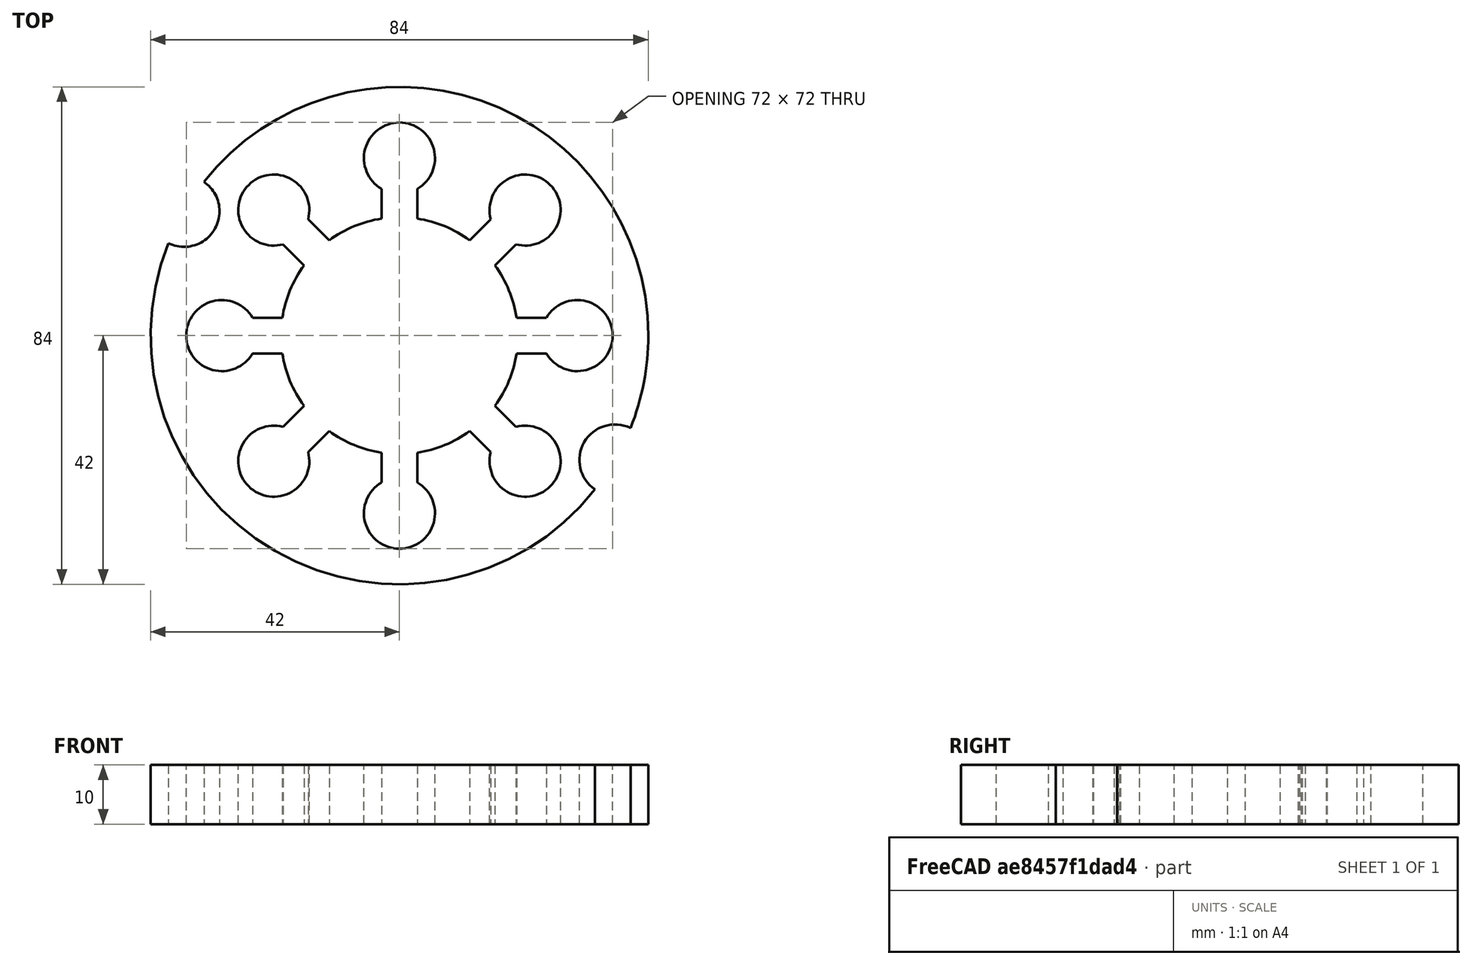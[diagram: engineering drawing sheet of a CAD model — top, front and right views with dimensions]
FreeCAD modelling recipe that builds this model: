
FCSTD DOCUMENT  (FreeCAD 0.18R4 (GitTag))
Label: Assignment 3 Templates 2
License: All rights reserved
LicenseURL: http://en.wikipedia.org/wiki/All_rights_reserved
objects: TechDraw::DrawViewDimension×8, TechDraw::DrawViewAnnotation×4, Sketcher::SketchObject×3, TechDraw::DrawViewPart×3, PartDesign::Pocket×2, PartDesign::Pad×1, PartDesign::PolarPattern×1, PartDesign::Body×1, TechDraw::DrawSVGTemplate×1, TechDraw::DrawPage×1
note: 11 computed .brp shape members not serialized (recipe doc carries the construction recipe); baked Part::Feature solids carry a one-line shape summary decoded from their .brp

FEATURE [Sketcher::SketchObject] Sketch
  MapMode = 5
  Support = -> [XY_Plane]
  sketch-geometry (2):
    g0: Circle CenterX=0 CenterY=0 CenterZ=0 NormalX=0 NormalY=0 NormalZ=1 AngleXU=0 Radius=42
    g1: Circle CenterX=0 CenterY=0 CenterZ=0 NormalX=0 NormalY=0 NormalZ=1 AngleXU=0 Radius=20
  constraints (4):
    c: Coincident(g0,g1)
    c: Coincident(g0,g-1)
    c: Radius(g0) = 42
    c: Radius(g1) = 20
FEATURE [PartDesign::Pad] Pad
  Length = 10
  Length2 = 100
  Profile = -> Sketch
  Type = 0
FEATURE [Sketcher::SketchObject] Sketch001
  MapMode = 5
  Placement = pos=(0,0,10) rot=(0,0,1;0rad)
  Support = -> [Pad]
  sketch-geometry (2):
    g0: Circle CenterX=-36.37 CenterY=21 CenterZ=0 NormalX=0 NormalY=0 NormalZ=1 AngleXU=0 Radius=6
    g1: Circle CenterX=36.37 CenterY=-21 CenterZ=0 NormalX=0 NormalY=0 NormalZ=1 AngleXU=0 Radius=6
  constraints (5):
    c: Symmetric(g1,g0,g-1)
    c: Radius(g1) = 6
    c: Radius(g0) = 6
    c: DistanceY(g-1,g0) = 21
    c: DistanceX(g-1,g1) = 36.37
FEATURE [PartDesign::Pocket] Pocket
  BaseFeature = -> Pad
  Length = 5
  Length2 = 100
  Profile = -> Sketch001
  Type = 1
FEATURE [Sketcher::SketchObject] Sketch002
  MapMode = 5
  Placement = pos=(0,0,10) rot=(0,0,1;0rad)
  Support = -> [Pocket]
  sketch-geometry (4):
    g0: ArcOfCircle CenterX=0 CenterY=30 CenterZ=0 NormalX=0 NormalY=0 NormalZ=1 AngleXU=0 Radius=6 StartAngle=5.23599 EndAngle=10.472
    g1: LineSegment StartX=-3 StartY=24.8038 StartZ=0 EndX=-3 EndY=19.7737 EndZ=0
    g2: LineSegment StartX=3 StartY=24.8038 StartZ=0 EndX=3 EndY=19.7737 EndZ=0
    g3: ArcOfCircle CenterX=0 CenterY=0 CenterZ=0 NormalX=0 NormalY=0 NormalZ=1 AngleXU=0 Radius=20 StartAngle=1.42023 EndAngle=1.72136
  constraints (12):
    c: Radius(g0) = 6
    c: DistanceY(g-1,g0) = 30
    c: PointOnObject(g0,g-2)
    c: Radius(g3) = 20
    c: Coincident(g-1,g3)
    c: Vertical(g1)
    c: Vertical(g2)
    c: PointOnObject(g0,g2)
    c: PointOnObject(g0,g1)
    c: Coincident(g3,g2)
    c: Coincident(g3,g1)
    c: DistanceX(g0,g0) = 6
FEATURE [PartDesign::Pocket] Pocket001
  BaseFeature = -> Pocket
  Length = 5
  Length2 = 100
  Profile = -> Sketch002
  Type = 1
FEATURE [PartDesign::PolarPattern] PolarPattern
  Angle = 360
  Axis = -> Sketch002 [N_Axis]
  BaseFeature = -> Pocket001
  Occurrences = 8
  Originals = -> [Pocket001]
FEATURE [PartDesign::Body] Body
  Group = -> [Sketch,Pad,Sketch001,Pocket,Sketch002,Pocket001,PolarPattern]
  Origin = -> Origin
  Tip = -> PolarPattern
FEATURE [TechDraw::DrawSVGTemplate] Template
  EditableTexts = Designed_by_Name=Soumojit Shome; Drawing_number=Drawing number- 03; FC-Date=15/11/2022; FC-SC=1:1; FC-SH=03; FC-Title=Academy of Technology; Subtitle=ECE-3 (X) ROLL - 139; Weight=Weight
  Height = 210
  Orientation = 1
  Width = 297
FEATURE [TechDraw::DrawViewPart] View
  CoarseView = false
  Direction = (0,0,1)
  Focus = 100
  HardHidden = false
  IsoCount = 0
  IsoHidden = false
  IsoVisible = false
  LockPosition = false
  Perspective = false
  Rotation = 0
  ScaleType = 0
  SeamHidden = false
  SeamVisible = false
  SmoothHidden = false
  SmoothVisible = false
  Source = -> [PolarPattern]
  X = 79.1917
  Y = 87.7641
FEATURE [TechDraw::DrawViewPart] View001
  CoarseView = false
  Direction = (0,-1,0)
  Focus = 100
  HardHidden = false
  IsoCount = 0
  IsoHidden = false
  IsoVisible = false
  LockPosition = false
  Perspective = false
  Rotation = 0
  ScaleType = 0
  SeamHidden = false
  SeamVisible = false
  SmoothHidden = false
  SmoothVisible = false
  Source = -> [PolarPattern]
  X = 77.2612
  Y = 182.602
FEATURE [TechDraw::DrawViewAnnotation] Annotation
  Font = osifont
  LineSpace = 80
  LockPosition = false
  MaxWidth = -1
  Rotation = 0
  ScaleType = 0
  Text = Front View
  TextSize = 6
  TextStyle = 0
  X = 78.4686
  Y = 164.472
FEATURE [TechDraw::DrawViewAnnotation] Annotation001
  Font = osifont
  LineSpace = 80
  LockPosition = false
  MaxWidth = -1
  Rotation = 0
  ScaleType = 0
  Text = Top View
  TextSize = 6
  TextStyle = 0
  X = 79.0471
  Y = 28.4477
FEATURE [TechDraw::DrawViewPart] View002
  CoarseView = false
  Direction = (0.577,-0.577,0.577)
  Focus = 100
  HardHidden = false
  IsoCount = 0
  IsoHidden = false
  IsoVisible = false
  LockPosition = false
  Perspective = false
  Rotation = 0
  ScaleType = 0
  SeamHidden = false
  SeamVisible = false
  SmoothHidden = false
  SmoothVisible = false
  Source = -> [PolarPattern]
  X = 217.907
  Y = 138.113
FEATURE [TechDraw::DrawViewAnnotation] Annotation002
  Font = osifont
  LineSpace = 80
  LockPosition = false
  MaxWidth = -1
  Rotation = 0
  ScaleType = 0
  Text = Isometric View
  TextSize = 6
  TextStyle = 0
  X = 220.835
  Y = 91.701
FEATURE [TechDraw::DrawViewDimension] Dimension
  Arbitrary = false
  FormatSpec = %.2f
  LockPosition = false
  MeasureType = 1
  OverTolerance = 0
  References2D = -> [View001]
  Rotation = 0
  ScaleType = 0
  Type = 2
  UnderTolerance = 0
  X = 59.4308
  Y = -17.4308
FEATURE [TechDraw::DrawViewDimension] Dimension001
  Arbitrary = false
  FormatSpec = R%.2f
  LockPosition = false
  MeasureType = 1
  OverTolerance = 0
  References2D = -> [View]
  Rotation = 0
  ScaleType = 0
  Type = 4
  UnderTolerance = 0
  X = 60.0269
  Y = 48.1297
FEATURE [TechDraw::DrawViewDimension] Dimension002
  Arbitrary = false
  FormatSpec = R%.2f
  LockPosition = false
  MeasureType = 1
  OverTolerance = 0
  References2D = -> [View]
  Rotation = 0
  ScaleType = 0
  Type = 4
  UnderTolerance = 0
  X = 58.9453
  Y = 37.5844
FEATURE [TechDraw::DrawViewDimension] Dimension003
  Arbitrary = false
  FormatSpec = R%.2f
  LockPosition = false
  MeasureType = 1
  OverTolerance = 0
  References2D = -> [View]
  Rotation = 0
  ScaleType = 0
  Type = 4
  UnderTolerance = 0
  X = 60.0269
  Y = 19.1978
FEATURE [TechDraw::DrawViewDimension] Dimension006
  Arbitrary = false
  FormatSpec = R%.2f
  LockPosition = false
  MeasureType = 1
  OverTolerance = 0
  References2D = -> [View]
  Rotation = 0
  ScaleType = 0
  Type = 4
  UnderTolerance = 0
  X = 63.8124
  Y = -18.3866
FEATURE [TechDraw::DrawViewDimension] Dimension007
  Arbitrary = false
  FormatSpec = %.2f
  LockPosition = false
  MeasureType = 1
  OverTolerance = 0
  References2D = -> [View]
  Rotation = 0
  ScaleType = 0
  Type = 1
  UnderTolerance = 0
  X = 13.2492
  Y = 54.1134
FEATURE [TechDraw::DrawViewDimension] Dimension008
  Arbitrary = false
  FormatSpec = %.2f
  LockPosition = false
  MeasureType = 1
  OverTolerance = 0
  References2D = -> [View]
  Rotation = 0
  ScaleType = 0
  Type = 7
  UnderTolerance = 0
  X = -60.5677
  Y = 17.0347
FEATURE [TechDraw::DrawViewDimension] Dimension009
  Arbitrary = false
  FormatSpec = %.2f
  LockPosition = false
  MeasureType = 1
  OverTolerance = 0
  References2D = -> [View]
  Rotation = 0
  ScaleType = 0
  Type = 2
  UnderTolerance = 0
  X = -56.5118
  Y = -16.6223
FEATURE [TechDraw::DrawViewAnnotation] Annotation003
  Font = osifont
  LineSpace = 80
  LockPosition = false
  MaxWidth = -1
  Rotation = 0
  ScaleType = 0
  Text = Template2 
  TextSize = 6
  TextStyle = 0
  X = 207.986
  Y = 30.6424
FEATURE [TechDraw::DrawPage] Page
  KeepUpdated = true
  ProjectionType = 0
  Template = -> Template
  Views = -> [View,View001,Annotation,Annotation001,View002,Annotation002,Dimension,Dimension001,Dimension002,Dimension003,Dimension006,Dimension007,Dimension008,Dimension009,Annotation003]
